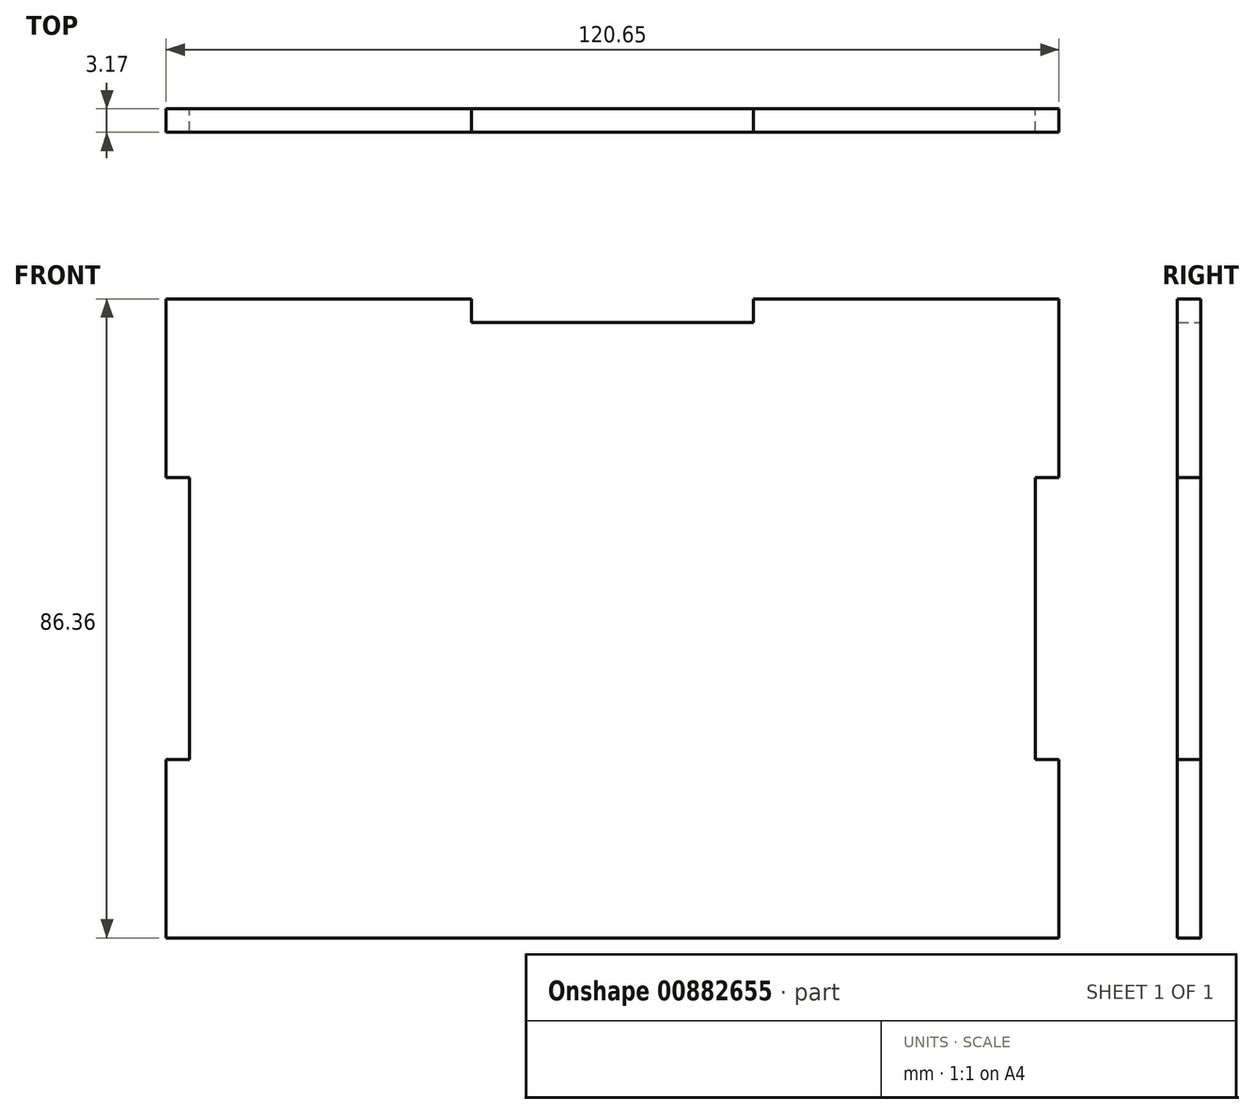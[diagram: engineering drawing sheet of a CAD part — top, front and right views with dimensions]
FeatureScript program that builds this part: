
annotation { "Feature Type Name" : "Feature", "Feature Type Description" : "" }
export const myFeature = defineFeature(function(context is Context, id is Id, definition is map)
    precondition{}
    {
        {
            var Q0;
            Q0=qCreatedBy(makeId("Front.planeOp"),FACE);
            var sketch = newSketch(context, id + "F0", { "sketchPlane" : qUnion([Q0])});
            skLineSegment(sketch, "E0.bottom", {"start": v(60.32, -43.18) * mm, "end": v(-60.33, -43.18) * mm});
            skLineSegment(sketch, "E0.top", {"start": v(60.33, 43.18) * mm, "end": v(-60.33, 43.18) * mm});
            skLineSegment(sketch, "E0.left", {"start": v(60.33, -43.18) * mm, "end": v(60.33, 43.18) * mm});
            skLineSegment(sketch, "E0.right", {"start": v(-60.33, -43.18) * mm, "end": v(-60.33, 43.18) * mm});
            skPoint(sketch, "E0.middle", {"position": v(0, 0) * mm});
            skLineSegment(sketch, "E1", {"start": v(0, 43.18) * mm, "end": v(-19.05, 43.18) * mm});
            skLineSegment(sketch, "E2", {"start": v(0, 43.18) * mm, "end": v(19.05, 43.18) * mm});
            skLineSegment(sketch, "E3", {"start": v(19.05, 43.18) * mm, "end": v(19.05, 40) * mm});
            skLineSegment(sketch, "E4", {"start": v(19.05, 40) * mm, "end": v(-19.05, 40) * mm});
            skLineSegment(sketch, "E5", {"start": v(-19.05, 40) * mm, "end": v(-19.05, 43.18) * mm});
            skLineSegment(sketch, "E6", {"start": v(-60.33, 0) * mm, "end": v(-60.33, 19.05) * mm});
            skLineSegment(sketch, "E7", {"start": v(-60.33, 0) * mm, "end": v(-60.33, -19.05) * mm});
            skLineSegment(sketch, "E8", {"start": v(-60.33, -19.05) * mm, "end": v(-57.15, -19.05) * mm});
            skLineSegment(sketch, "E9", {"start": v(-60.33, 19.05) * mm, "end": v(-57.15, 19.05) * mm});
            skLineSegment(sketch, "E10", {"start": v(-57.15, 19.05) * mm, "end": v(-57.15, -19.05) * mm});
            skLineSegment(sketch, "E11", {"start": v(0, 0) * mm, "end": v(0, -43.18) * mm});
            skLineSegment(sketch, "E12", {"start": v(0, -43.18) * mm, "end": v(0, 43.18) * mm});
            skLineSegment(sketch, "E13.MirrorCS", {"start": v(57.15, 19.05) * mm, "end": v(57.15, -19.05) * mm});
            skLineSegment(sketch, "E14", {"start": v(57.15, 19.05) * mm, "end": v(60.33, 19.05) * mm});
            skLineSegment(sketch, "E15", {"start": v(57.15, -19.05) * mm, "end": v(60.33, -19.05) * mm});
            skSolve(sketch);
        }
        {
            var Q0;
            Q0=makeQuery(id+"F0.imprint","IMPRINT",FACE,{"disambiguationData":[TD([[makeQuery(id+"F0.imprint","IMPRINT",EDGE,{"derivedFrom":sQuery(id+"F0.wireOp",EDGE,"E0.bottom")}),-1.0]])]});
            extrude(context, id + "F1", {"entities" : qUnion([Q0]), "depth" : 3.17 * mm, "offsetDistance" : 25.4 * mm});
        }
    });
